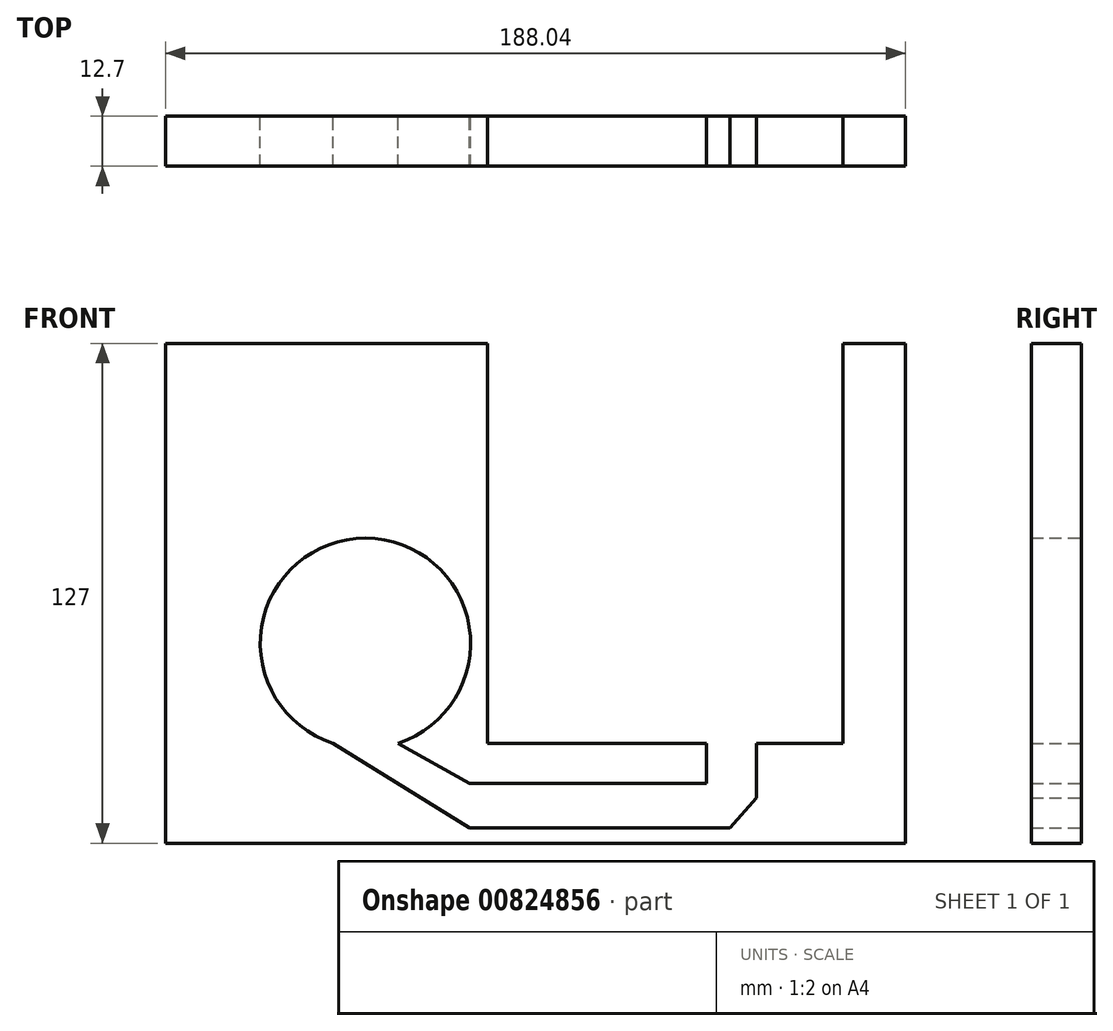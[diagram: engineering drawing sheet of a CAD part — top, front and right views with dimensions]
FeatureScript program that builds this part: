
annotation { "Feature Type Name" : "Feature", "Feature Type Description" : "" }
export const myFeature = defineFeature(function(context is Context, id is Id, definition is map)
    precondition{}
    {
        {
            var Q0;
            Q0=qCreatedBy(makeId("Front.planeOp"),FACE);
            var sketch = newSketch(context, id + "F0", { "sketchPlane" : qUnion([Q0])});
            skLineSegment(sketch, "E0", {"start": v(-90.94, 101.6) * mm, "end": v(-90.94, -25.4) * mm});
            skLineSegment(sketch, "E1", {"start": v(-90.94, -25.4) * mm, "end": v(97.1, -25.4) * mm});
            skLineSegment(sketch, "E2", {"start": v(97.1, -25.4) * mm, "end": v(97.1, 101.6) * mm});
            skLineSegment(sketch, "E3", {"start": v(97.1, 101.6) * mm, "end": v(81.23, 101.6) * mm});
            skLineSegment(sketch, "E4", {"start": v(81.23, 101.6) * mm, "end": v(81.23, 0) * mm});
            skLineSegment(sketch, "E5", {"start": v(81.23, 0) * mm, "end": v(59.26, 0) * mm});
            skLineSegment(sketch, "E6", {"start": v(59.26, 0) * mm, "end": v(59.26, -13.88) * mm});
            skLineSegment(sketch, "E7", {"start": v(59.26, -13.88) * mm, "end": v(52.47, -21.48) * mm});
            skLineSegment(sketch, "E8", {"start": v(-90.94, 101.6) * mm, "end": v(-9.13, 101.6) * mm});
            skLineSegment(sketch, "E9", {"start": v(-9.13, 101.6) * mm, "end": v(-9.13, 0) * mm});
            skLineSegment(sketch, "E10", {"start": v(-9.13, 0) * mm, "end": v(46.56, 0) * mm});
            skLineSegment(sketch, "E11", {"start": v(46.56, 0) * mm, "end": v(46.56, -10.2) * mm});
            skLineSegment(sketch, "E12", {"start": v(46.56, -10.2) * mm, "end": v(-13.74, -10.2) * mm});
            skLineSegment(sketch, "E13", {"start": v(-13.74, -10.2) * mm, "end": v(-31.87, 0) * mm});
            skLineSegment(sketch, "E14", {"start": v(52.47, -21.48) * mm, "end": v(-13.74, -21.48) * mm});
            skLineSegment(sketch, "E15", {"start": v(-13.74, -21.48) * mm, "end": v(-48.4, 0) * mm});
            skArc(sketch, "E16", {"start": v(-31.87, 0) * mm, "mid": v(-40.14, 52.11) * mm, "end": v(-48.4, 0) * mm});
            skSolve(sketch);
        }
        {
            var Q0;
            Q0=qSketchRegion(id+"F0",true);
            extrude(context, id + "F1", {"entities" : qUnion([Q0]), "depth" : 12.7 * mm, "offsetDistance" : 25.4 * mm});
        }
    });
